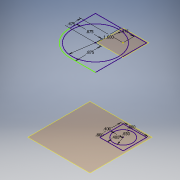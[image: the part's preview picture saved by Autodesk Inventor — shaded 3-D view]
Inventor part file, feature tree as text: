
AUTODESK INVENTOR PART (.ipt)
format: ipt  version: 2018 (Build 220112000, 112)  size: 101,376 bytes
history: native  units: in
note: dims shown in document units (in); Inventor stores cm internally (conversion verified against a paired STEP export)
features: sketch x2, plane x1
ambient origin geometry x8: Origin, YZ Plane, XZ Plane, XY Plane, X Axis, Y Axis, Z Axis, Center Point
feature tree (3):
  sketch  "Sketch1"  dims[d0=0.65in]
  plane  "Work Plane1"
  sketch  "Sketch2"  dims[d1=0.8in d2=0.8in d3=0.4in d4=0.4in d5=2.8in d6=1.6in d7=0.475in d8=0.475in d9=0.875in d10=0.875in]
